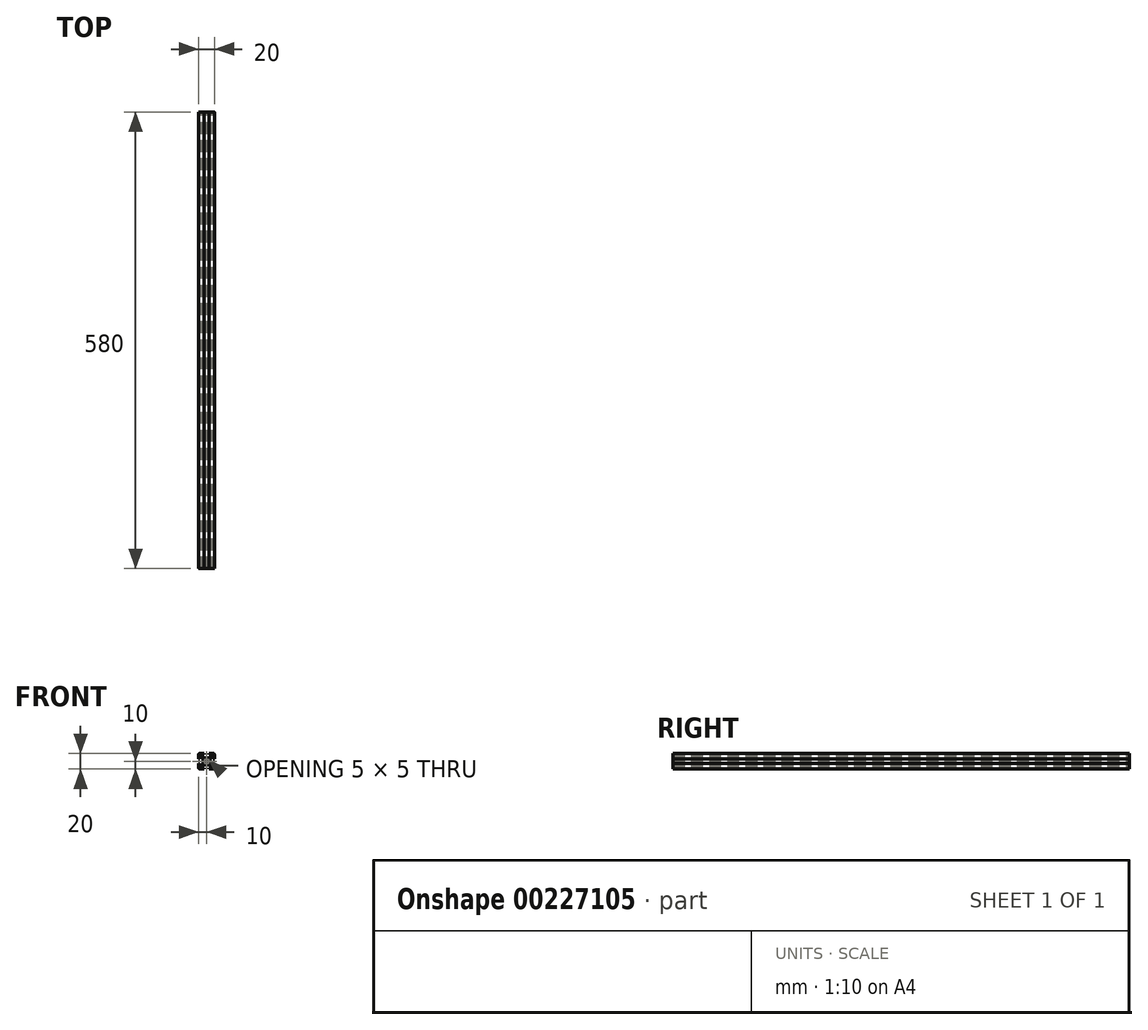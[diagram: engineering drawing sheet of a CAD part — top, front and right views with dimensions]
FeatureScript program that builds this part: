
annotation { "Feature Type Name" : "Feature", "Feature Type Description" : "" }
export const myFeature = defineFeature(function(context is Context, id is Id, definition is map)
    precondition{}
    {
        {
            var Q0;
            Q0=qCreatedBy(makeId("Front.planeOp"),FACE);
            var sketch = newSketch(context, id + "F0", { "sketchPlane" : qUnion([Q0])});
            skLineSegment(sketch, "E0.bottom", {"start": v(8.5, -10) * mm, "end": v(3, -10) * mm});
            skLineSegment(sketch, "E0.top", {"start": v(8.5, 10) * mm, "end": v(3, 10) * mm});
            skLineSegment(sketch, "E0.left", {"start": v(10, -8.5) * mm, "end": v(10, -3) * mm});
            skLineSegment(sketch, "E0.right", {"start": v(-10, -8.5) * mm, "end": v(-10, -3) * mm});
            skPoint(sketch, "E0.middle", {"position": v(0, 0) * mm});
            skLineSegment(sketch, "E1.bottom", {"start": v(6, -8.5) * mm, "end": v(3, -8.5) * mm});
            skLineSegment(sketch, "E1.top", {"start": v(6, 8.5) * mm, "end": v(3, 8.5) * mm});
            skLineSegment(sketch, "E1.left", {"start": v(8.5, -6) * mm, "end": v(8.5, -3) * mm});
            skLineSegment(sketch, "E1.right", {"start": v(-8.5, -6) * mm, "end": v(-8.5, -3) * mm});
            skLineSegment(sketch, "E2.bottom", {"start": v(3.44, -4.5) * mm, "end": v(-3.44, -4.5) * mm});
            skLineSegment(sketch, "E2.top", {"start": v(3.44, 4.5) * mm, "end": v(-3.44, 4.5) * mm});
            skLineSegment(sketch, "E2.left", {"start": v(4.5, -3.44) * mm, "end": v(4.5, 3.44) * mm});
            skLineSegment(sketch, "E2.right", {"start": v(-4.5, -3.44) * mm, "end": v(-4.5, 3.44) * mm});
            skLineSegment(sketch, "E3.bottom", {"start": v(8.5, -6) * mm, "end": v(7.06, -6) * mm});
            skLineSegment(sketch, "E3.top", {"start": v(8.5, 6) * mm, "end": v(7.06, 6) * mm});
            skLineSegment(sketch, "E4.left", {"start": v(6, -8.5) * mm, "end": v(6, -7.06) * mm});
            skLineSegment(sketch, "E4.right", {"start": v(-6, -8.5) * mm, "end": v(-6, -7.06) * mm});
            skPoint(sketch, "E5.orphan", {"position": v(-8.5, 8.5) * mm});
            skPoint(sketch, "E6.orphan", {"position": v(8.5, 8.5) * mm});
            skPoint(sketch, "E7.orphan", {"position": v(8.5, -8.5) * mm});
            skPoint(sketch, "E8.orphan", {"position": v(-8.5, -8.5) * mm});
            skLineSegment(sketch, "E9.trimOffspring", {"start": v(-6, 7.06) * mm, "end": v(-6, 8.5) * mm});
            skLineSegment(sketch, "E10.trimOffspring", {"start": v(-7.06, 6) * mm, "end": v(-8.5, 6) * mm});
            skLineSegment(sketch, "E11.trimOffspring", {"start": v(6, 7.06) * mm, "end": v(6, 8.5) * mm});
            skLineSegment(sketch, "E12.trimOffspring", {"start": v(-7.06, -6) * mm, "end": v(-8.5, -6) * mm});
            skLineSegment(sketch, "E13", {"start": v(-10, 10) * mm, "end": v(0, 0) * mm, "construction": true});
            skLineSegment(sketch, "E14", {"start": v(10, 10) * mm, "end": v(0, 0) * mm, "construction": true});
            skLineSegment(sketch, "E15", {"start": v(-6, 7.06) * mm, "end": v(-3.44, 4.5) * mm});
            skPoint(sketch, "E15.endSnap0", {"position": v(7.25, -6) * mm});
            skLineSegment(sketch, "E16", {"start": v(6, -7.06) * mm, "end": v(3.44, -4.5) * mm});
            skLineSegment(sketch, "E17", {"start": v(7.06, 6) * mm, "end": v(4.5, 3.44) * mm});
            skLineSegment(sketch, "E18", {"start": v(6, 7.06) * mm, "end": v(3.44, 4.5) * mm});
            skPoint(sketch, "E19.orphan", {"position": v(6, -6) * mm});
            skPoint(sketch, "E20.orphan", {"position": v(-4.5, -4.5) * mm});
            skPoint(sketch, "E21.orphan", {"position": v(-4.5, 4.5) * mm});
            skPoint(sketch, "E22.orphan", {"position": v(4.5, 4.5) * mm});
            skPoint(sketch, "E23.orphan", {"position": v(4.5, -4.5) * mm});
            skLineSegment(sketch, "E24.trimOffspring", {"start": v(4.5, -3.44) * mm, "end": v(7.06, -6) * mm});
            skLineSegment(sketch, "E25.trimOffspring", {"start": v(-3.44, -4.5) * mm, "end": v(-6, -7.06) * mm});
            skLineSegment(sketch, "E26.trimOffspring", {"start": v(-4.5, -3.44) * mm, "end": v(-7.06, -6) * mm});
            skLineSegment(sketch, "E27.trimOffspring", {"start": v(-4.5, 3.44) * mm, "end": v(-7.06, 6) * mm});
            skLineSegment(sketch, "E28.bottom", {"start": v(8.5, -3) * mm, "end": v(10, -3) * mm});
            skLineSegment(sketch, "E28.top", {"start": v(8.5, 3) * mm, "end": v(10, 3) * mm});
            skPoint(sketch, "E28.middle", {"position": v(10, 0) * mm});
            skLineSegment(sketch, "E29.left", {"start": v(3, 8.5) * mm, "end": v(3, 10) * mm});
            skLineSegment(sketch, "E29.right", {"start": v(-3, 8.5) * mm, "end": v(-3, 10) * mm});
            skPoint(sketch, "E29.middle", {"position": v(0, 10) * mm});
            skLineSegment(sketch, "E30.bottom", {"start": v(-8.5, 3) * mm, "end": v(-10, 3) * mm});
            skLineSegment(sketch, "E30.top", {"start": v(-8.5, -3) * mm, "end": v(-10, -3) * mm});
            skPoint(sketch, "E30.middle", {"position": v(-10, 0) * mm});
            skLineSegment(sketch, "E31.left", {"start": v(3, -8.5) * mm, "end": v(3, -10) * mm});
            skLineSegment(sketch, "E31.right", {"start": v(-3, -8.5) * mm, "end": v(-3, -10) * mm});
            skPoint(sketch, "E31.middle", {"position": v(0, -10) * mm});
            skPoint(sketch, "E32.orphan", {"position": v(3, 11.5) * mm});
            skPoint(sketch, "E33.orphan", {"position": v(-3, 11.5) * mm});
            skLineSegment(sketch, "E34.trimOffspring", {"start": v(-3, 10) * mm, "end": v(-8.5, 10) * mm});
            skLineSegment(sketch, "E35.trimOffspring", {"start": v(-3, 8.5) * mm, "end": v(-6, 8.5) * mm});
            skPoint(sketch, "E28.right.end.orphan", {"position": v(11.5, 3) * mm});
            skPoint(sketch, "E36.orphan", {"position": v(11.5, -3) * mm});
            skLineSegment(sketch, "E37.trimOffspring", {"start": v(10, 3) * mm, "end": v(10, 8.5) * mm});
            skLineSegment(sketch, "E38.trimOffspring", {"start": v(8.5, 3) * mm, "end": v(8.5, 6) * mm});
            skPoint(sketch, "E39.orphan", {"position": v(3, -11.5) * mm});
            skPoint(sketch, "E40.orphan", {"position": v(-3, -11.5) * mm});
            skLineSegment(sketch, "E41.trimOffspring", {"start": v(-3, -10) * mm, "end": v(-8.5, -10) * mm});
            skLineSegment(sketch, "E42.trimOffspring", {"start": v(-3, -8.5) * mm, "end": v(-6, -8.5) * mm});
            skPoint(sketch, "E30.right.end.orphan", {"position": v(-11.5, -3) * mm});
            skPoint(sketch, "E43.orphan", {"position": v(-11.5, 3) * mm});
            skLineSegment(sketch, "E44.trimOffspring", {"start": v(-10, 3) * mm, "end": v(-10, 8.5) * mm});
            skLineSegment(sketch, "E45.trimOffspring", {"start": v(-8.5, 3) * mm, "end": v(-8.5, 6) * mm});
            skLineSegment(sketch, "E46.trimOffspring", {"start": v(0, 0) * mm, "end": v(10, -10) * mm, "construction": true});
            skLineSegment(sketch, "E47.trimOffspring", {"start": v(0, 0) * mm, "end": v(-10, -10) * mm, "construction": true});
            skArc(sketch, "E48", {"start": v(1.16, 2.22) * mm, "mid": v(0, 2.5) * mm, "end": v(-1.16, 2.22) * mm});
            skLineSegment(sketch, "E49", {"start": v(-2.5, -1.44) * mm, "end": v(1.44, 2.5) * mm});
            skLineSegment(sketch, "E50", {"start": v(2.5, 1.44) * mm, "end": v(-1.44, -2.5) * mm});
            skLineSegment(sketch, "E51", {"start": v(1.44, -2.5) * mm, "end": v(-2.5, 1.44) * mm});
            skLineSegment(sketch, "E52", {"start": v(-1.44, 2.5) * mm, "end": v(2.5, -1.44) * mm});
            skLineSegment(sketch, "E53", {"start": v(2.5, 1.44) * mm, "end": v(2.5, -1.44) * mm, "construction": true});
            skLineSegment(sketch, "E54", {"start": v(1.44, -2.5) * mm, "end": v(-1.44, -2.5) * mm, "construction": true});
            skLineSegment(sketch, "E55", {"start": v(-2.5, -1.44) * mm, "end": v(-2.5, 1.44) * mm, "construction": true});
            skLineSegment(sketch, "E56", {"start": v(-1.44, 2.5) * mm, "end": v(1.44, 2.5) * mm, "construction": true});
            skLineSegment(sketch, "E57", {"start": v(-1.44, 2.5) * mm, "end": v(-2.5, 1.44) * mm});
            skLineSegment(sketch, "E58", {"start": v(1.44, 2.5) * mm, "end": v(2.5, 1.44) * mm});
            skLineSegment(sketch, "E59", {"start": v(2.5, -1.44) * mm, "end": v(1.44, -2.5) * mm});
            skLineSegment(sketch, "E60", {"start": v(-1.44, -2.5) * mm, "end": v(-2.5, -1.44) * mm});
            skArc(sketch, "E61.trimOffspring", {"start": v(-2.22, 1.16) * mm, "mid": v(-2.5, 0) * mm, "end": v(-2.22, -1.16) * mm});
            skArc(sketch, "E62.trimOffspring", {"start": v(-1.16, -2.22) * mm, "mid": v(0, -2.5) * mm, "end": v(1.16, -2.22) * mm});
            skArc(sketch, "E63.trimOffspring", {"start": v(2.22, -1.16) * mm, "mid": v(2.5, 0) * mm, "end": v(2.22, 1.16) * mm});
            skPoint(sketch, "E64.visualSharp", {"position": v(10, 10) * mm});
            skArc(sketch, "E64.filletArc", {"start": v(10, 8.5) * mm, "mid": v(9.56, 9.56) * mm, "end": v(8.5, 10) * mm});
            skPoint(sketch, "E65.visualSharp", {"position": v(10, -10) * mm});
            skArc(sketch, "E65.filletArc", {"start": v(8.5, -10) * mm, "mid": v(9.56, -9.56) * mm, "end": v(10, -8.5) * mm});
            skPoint(sketch, "E66.visualSharp", {"position": v(-10, -10) * mm});
            skArc(sketch, "E66.filletArc", {"start": v(-10, -8.5) * mm, "mid": v(-9.56, -9.56) * mm, "end": v(-8.5, -10) * mm});
            skPoint(sketch, "E67.visualSharp", {"position": v(-10, 10) * mm});
            skArc(sketch, "E67.filletArc", {"start": v(-8.5, 10) * mm, "mid": v(-9.56, 9.56) * mm, "end": v(-10, 8.5) * mm});
            skSolve(sketch);
        }
        {
            assignVariable(context, id + "F2", {"name" : "Length", "anyValue" : 580});
        }
        {
            var Q0;
            Q0=qSketchRegion(id+"F0",true);
            extrude(context, id + "F1", {"entities" : qUnion([Q0]), "depth" : (getVariable(context, 'Length')) * mm});
        }
    });
